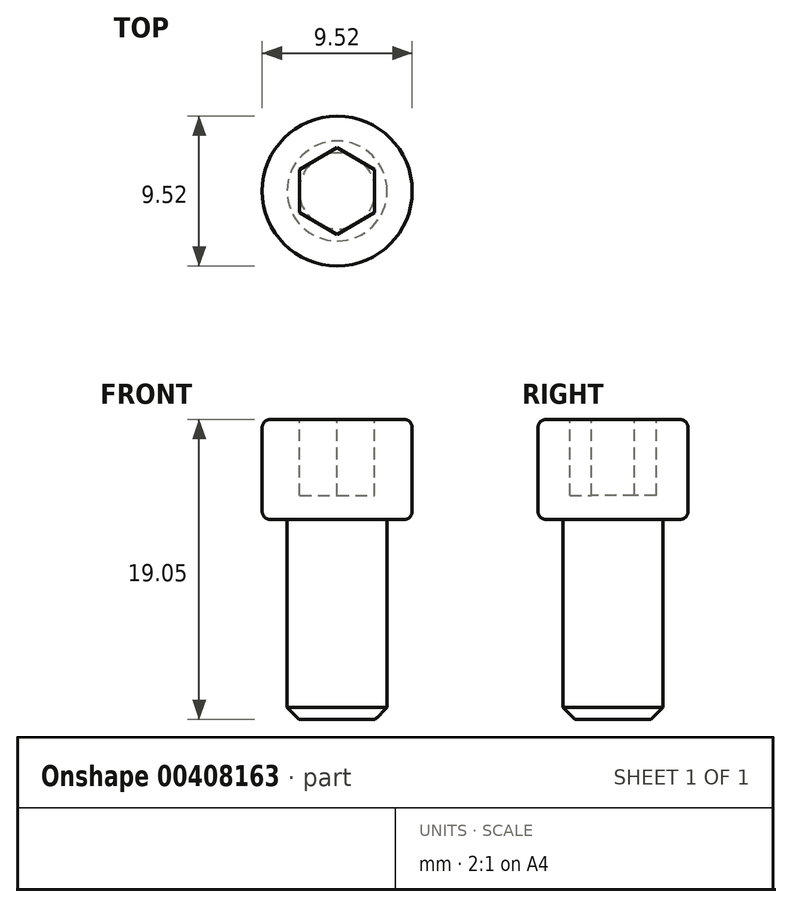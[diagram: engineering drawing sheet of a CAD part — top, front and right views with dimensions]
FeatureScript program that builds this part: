
annotation { "Feature Type Name" : "Feature", "Feature Type Description" : "" }
export const myFeature = defineFeature(function(context is Context, id is Id, definition is map)
    precondition{}
    {
        {
            var Q0;
            Q0=qCreatedBy(makeId("Top.planeOp"),FACE);
            cPlane(context, id + "F0", {"entities" : qUnion([Q0]), "cplaneType" : CPlaneType.OFFSET, "offset" : ((1 / 20) * 2) * mm, "oppositeDirection" : true, "width" : 152.4 * mm, "height" : 152.4 * mm});
        }
        {
            var Q0;
            Q0=qCreatedBy(makeId("Top.planeOp"),FACE);
            var sketch = newSketch(context, id + "F1", { "sketchPlane" : qUnion([Q0])});
            skCircle(sketch, "E0", {"center": v(0, 0) * mm, "radius": 4.76 * mm});
            skSolve(sketch);
        }
        {
            var Q0;
            Q0=qCreatedBy(makeId("Top.planeOp"),FACE);
            var sketch = newSketch(context, id + "F2", { "sketchPlane" : qUnion([Q0])});
            skCircle(sketch, "E1", {"center": v(0, 0) * mm, "radius": 3.18 * mm});
            skSolve(sketch);
        }
        {
            var Q0;
            Q0=qCreatedBy(id+"F0.planeOp",FACE);
            var sketch = newSketch(context, id + "F3", { "sketchPlane" : qUnion([Q0])});
            skCircle(sketch, "E2", {"center": v(0, 0) * mm, "radius": 2.38 * mm});
            skSolve(sketch);
        }
        {
            var Q0;
            Q0=makeQuery(id+"F1.imprint","IMPRINT",FACE,{"disambiguationData":[TD([[makeQuery(id+"F1.imprint","IMPRINT",EDGE,{"derivedFrom":sQuery(id+"F1.wireOp",EDGE,"E0")}),1.0]])]});
            extrude(context, id + "F4", {"entities" : qUnion([Q0]), "depth" : 6.35 * mm});
        }
        {
            var Q0;
            Q0=makeQuery(id+"F4.opExtrude","CAP_FACE",FACE,{"disambiguationData":[OSD([sQuery(id+"F1.wireOp",EDGE,"E0")])],"isStart":false});
            var sketch = newSketch(context, id + "F5", { "sketchPlane" : qUnion([Q0])});
            skCircle(sketch, "E3.cCircle", {"center": v(0, 0) * mm, "radius": 2.38 * mm, "construction": true});
            skLineSegment(sketch, "E3.0", {"start": v(2.38, 1.37) * mm, "end": v(2.38, -1.37) * mm});
            skLineSegment(sketch, "E3.1", {"start": v(2.38, -1.37) * mm, "end": v(0, -2.75) * mm});
            skLineSegment(sketch, "E3.2", {"start": v(0, -2.75) * mm, "end": v(-2.38, -1.37) * mm});
            skLineSegment(sketch, "E3.3", {"start": v(-2.38, -1.37) * mm, "end": v(-2.38, 1.37) * mm});
            skLineSegment(sketch, "E3.4", {"start": v(-2.38, 1.37) * mm, "end": v(0, 2.75) * mm});
            skLineSegment(sketch, "E3.5", {"start": v(0, 2.75) * mm, "end": v(2.38, 1.37) * mm});
            skPoint(sketch, "E3.0.midPoint", {"position": v(2.38, 0) * mm});
            skSolve(sketch);
        }
        {
            var Q0;
            Q0=makeQuery(id+"F5.imprint","IMPRINT",FACE,{"disambiguationData":[TD([[makeQuery(id+"F5.imprint","IMPRINT",EDGE,{"derivedFrom":sQuery(id+"F5.wireOp",EDGE,"E3.0")}),-1.0]])]});
            extrude(context, id + "F6", {"entities" : qUnion([Q0]), "operationType" : NewBodyOperationType.REMOVE, "oppositeDirection" : true, "depth" : 4.83 * mm});
        }
        {
            var Q0;
            Q0=makeQuery(id+"F2.imprint","IMPRINT",FACE,{"disambiguationData":[TD([[makeQuery(id+"F2.imprint","IMPRINT",EDGE,{"derivedFrom":sQuery(id+"F2.wireOp",EDGE,"E1")}),1.0]])]});
            extrude(context, id + "F7", {"entities" : qUnion([Q0]), "operationType" : NewBodyOperationType.ADD, "oppositeDirection" : true, "depth" : 12.7 * mm});
        }
        {
            var Q0;
            Q0=sQuery(id+"F3.wireOp",EDGE,"E2");
            var Q1;
            Q1=makeQuery(id+"F7.opExtrude","CAP_FACE",FACE,{"disambiguationData":[OSD([sQuery(id+"F2.wireOp",EDGE,"E1")])],"isStart":false});
            extrude(context, id + "F8", {"bodyType" : ToolBodyType.SURFACE, "surfaceEntities" : qUnion([Q0]), "endBound" : BoundingType.UP_TO_SURFACE, "oppositeDirection" : true, "endBoundEntityFace" : qUnion([Q1]), "depth" : 25.4 * mm});
        }
        {
            var Q0;
            Q0=makeQuery(id+"F7.opExtrude","CAP_EDGE",EDGE,{"disambiguationData":[OSD([sQuery(id+"F2.wireOp",EDGE,"E1")])],"isStart":false});
            chamfer(context, id + "F9", {"entities" : qUnion([Q0]), "chamferType" : ChamferType.OFFSET_ANGLE, "width" : 0.76 * mm, "oppositeDirection" : false, "angle" : 45 * degree, "tangentPropagation" : true});
        }
        {
            var Q0;
            Q0=makeQuery(id+"F4.opExtrude","CAP_EDGE",EDGE,{"disambiguationData":[OSD([sQuery(id+"F1.wireOp",EDGE,"E0")])],"isStart":false});
            var Q1;
            Q1=makeQuery(id+"F4.opExtrude","CAP_EDGE",EDGE,{"disambiguationData":[OSD([sQuery(id+"F1.wireOp",EDGE,"E0")])],"isStart":true});
            fillet(context, id + "F10", {"entities" : qUnion([Q0, Q1]), "radius" : 0.5 * mm, "tangentPropagation" : true, "allowEdgeOverflow" : false});
        }
    });
